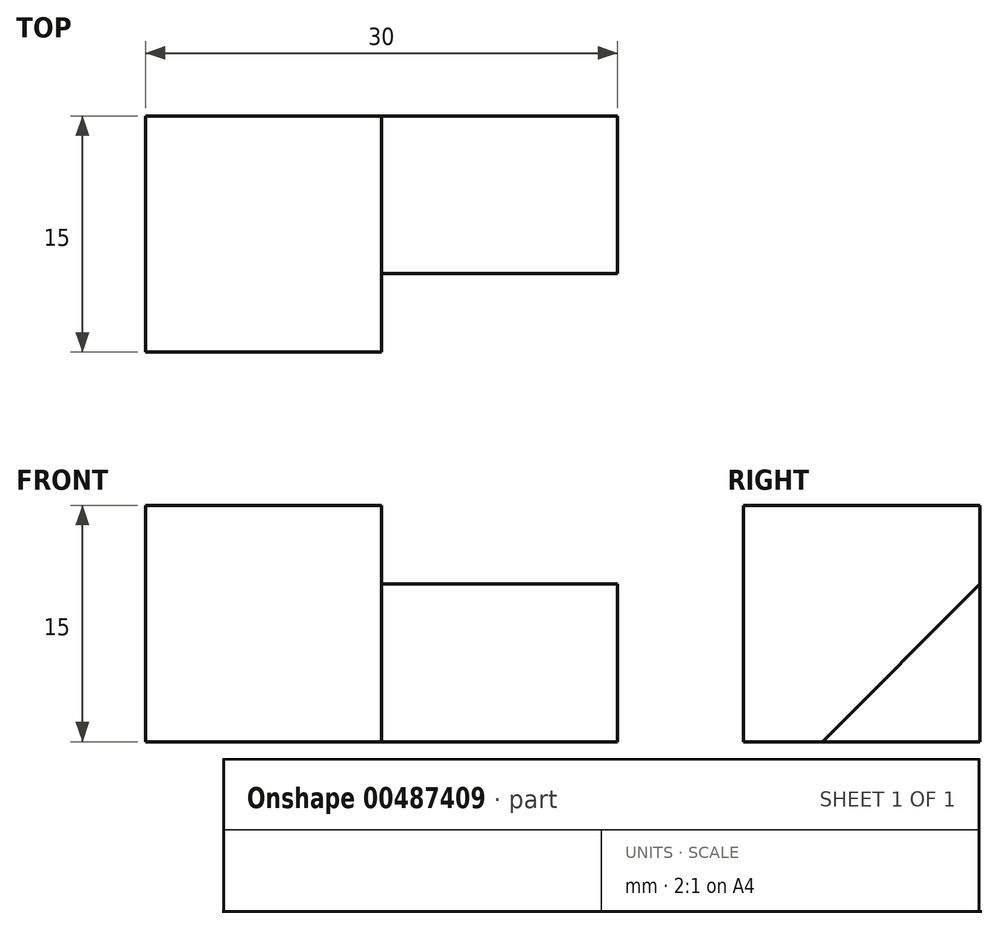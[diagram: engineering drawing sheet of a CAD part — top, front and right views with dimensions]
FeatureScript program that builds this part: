
annotation { "Feature Type Name" : "Feature", "Feature Type Description" : "" }
export const myFeature = defineFeature(function(context is Context, id is Id, definition is map)
    precondition{}
    {
        {
            var Q0;
            Q0=qCreatedBy(makeId("Top.planeOp"),FACE);
            var sketch = newSketch(context, id + "F0", { "sketchPlane" : qUnion([Q0])});
            skLineSegment(sketch, "E0.bottom", {"start": v(-26.46, -34.62) * mm, "end": v(3.54, -34.62) * mm});
            skLineSegment(sketch, "E0.top", {"start": v(-26.46, -49.62) * mm, "end": v(3.54, -49.62) * mm});
            skLineSegment(sketch, "E0.left", {"start": v(-26.46, -34.62) * mm, "end": v(-26.46, -49.62) * mm});
            skLineSegment(sketch, "E0.right", {"start": v(3.54, -34.62) * mm, "end": v(3.54, -49.62) * mm});
            skSolve(sketch);
        }
        {
            var Q0;
            Q0=makeQuery(id+"F0.imprint","IMPRINT",FACE,{"disambiguationData":[TD([[makeQuery(id+"F0.imprint","IMPRINT",EDGE,{"derivedFrom":sQuery(id+"F0.wireOp",EDGE,"E0.bottom")}),-1.0]])]});
            extrude(context, id + "F1", {"entities" : qUnion([Q0]), "depth" : 15 * mm});
        }
        {
            var Q0;
            Q0=makeQuery(id+"F1.opExtrude","SWEPT_FACE",FACE,{"disambiguationData":[OSD([sQuery(id+"F0.wireOp",EDGE,"E0.top")])]});
            var sketch = newSketch(context, id + "F2", { "sketchPlane" : qUnion([Q0])});
            skLineSegment(sketch, "E1", {"start": v(-11.46, 0) * mm, "end": v(-11.46, 15) * mm});
            skSolve(sketch);
        }
        {
            var Q0;
            {var subQ0=sQuery(id+"F2.wireOp",EDGE,"E1");Q0=makeQuery(id+"F2.imprint","IMPRINT",FACE,{"disambiguationData":[TD([[makeQuery(id+"F2.imprint","IMPRINT",EDGE,{"derivedFrom":subQ0}),-1.0]])]});}
            extrude(context, id + "F3", {"entities" : qUnion([Q0]), "operationType" : NewBodyOperationType.REMOVE, "oppositeDirection" : true, "depth" : 5 * mm});
        }
        {
            var Q0;
            Q0=makeQuery(id+"F1.opExtrude","SWEPT_FACE",FACE,{"disambiguationData":[OSD([sQuery(id+"F0.wireOp",EDGE,"E0.right")])]});
            var sketch = newSketch(context, id + "F4", { "sketchPlane" : qUnion([Q0])});
            skLineSegment(sketch, "E2", {"start": v(-34.62, 0) * mm, "end": v(-34.62, 10) * mm});
            skLineSegment(sketch, "E3", {"start": v(-34.62, 10) * mm, "end": v(-44.62, 10) * mm});
            skSolve(sketch);
        }
        {
            var Q0;
            {var subQ0=sQuery(id+"F4.wireOp",EDGE,"E3");Q0=makeQuery(id+"F4.imprint","IMPRINT",FACE,{"disambiguationData":[TD([[makeQuery(id+"F4.imprint","IMPRINT",EDGE,{"derivedFrom":subQ0}),-1.0]])]});}
            extrude(context, id + "F5", {"entities" : qUnion([Q0]), "operationType" : NewBodyOperationType.REMOVE, "oppositeDirection" : true, "depth" : 15 * mm});
        }
        {
            var Q0;
            Q0=makeQuery(id+"F1.opExtrude","SWEPT_FACE",FACE,{"disambiguationData":[OSD([sQuery(id+"F0.wireOp",EDGE,"E0.right")])]});
            var sketch = newSketch(context, id + "F6", { "sketchPlane" : qUnion([Q0])});
            skLineSegment(sketch, "E4", {"start": v(-44.62, 0) * mm, "end": v(-34.62, 10) * mm});
            skSolve(sketch);
        }
        {
            var Q0;
            Q0=makeQuery(id+"F6.imprint","IMPRINT",FACE,{"disambiguationData":[TD([[makeQuery(id+"F6.imprint","IMPRINT",EDGE,{"derivedFrom":sQuery(id+"F6.wireOp",EDGE,"E4")}),1.0]])]});
            extrude(context, id + "F7", {"entities" : qUnion([Q0]), "operationType" : NewBodyOperationType.REMOVE, "oppositeDirection" : true, "depth" : 15 * mm});
        }
    });
